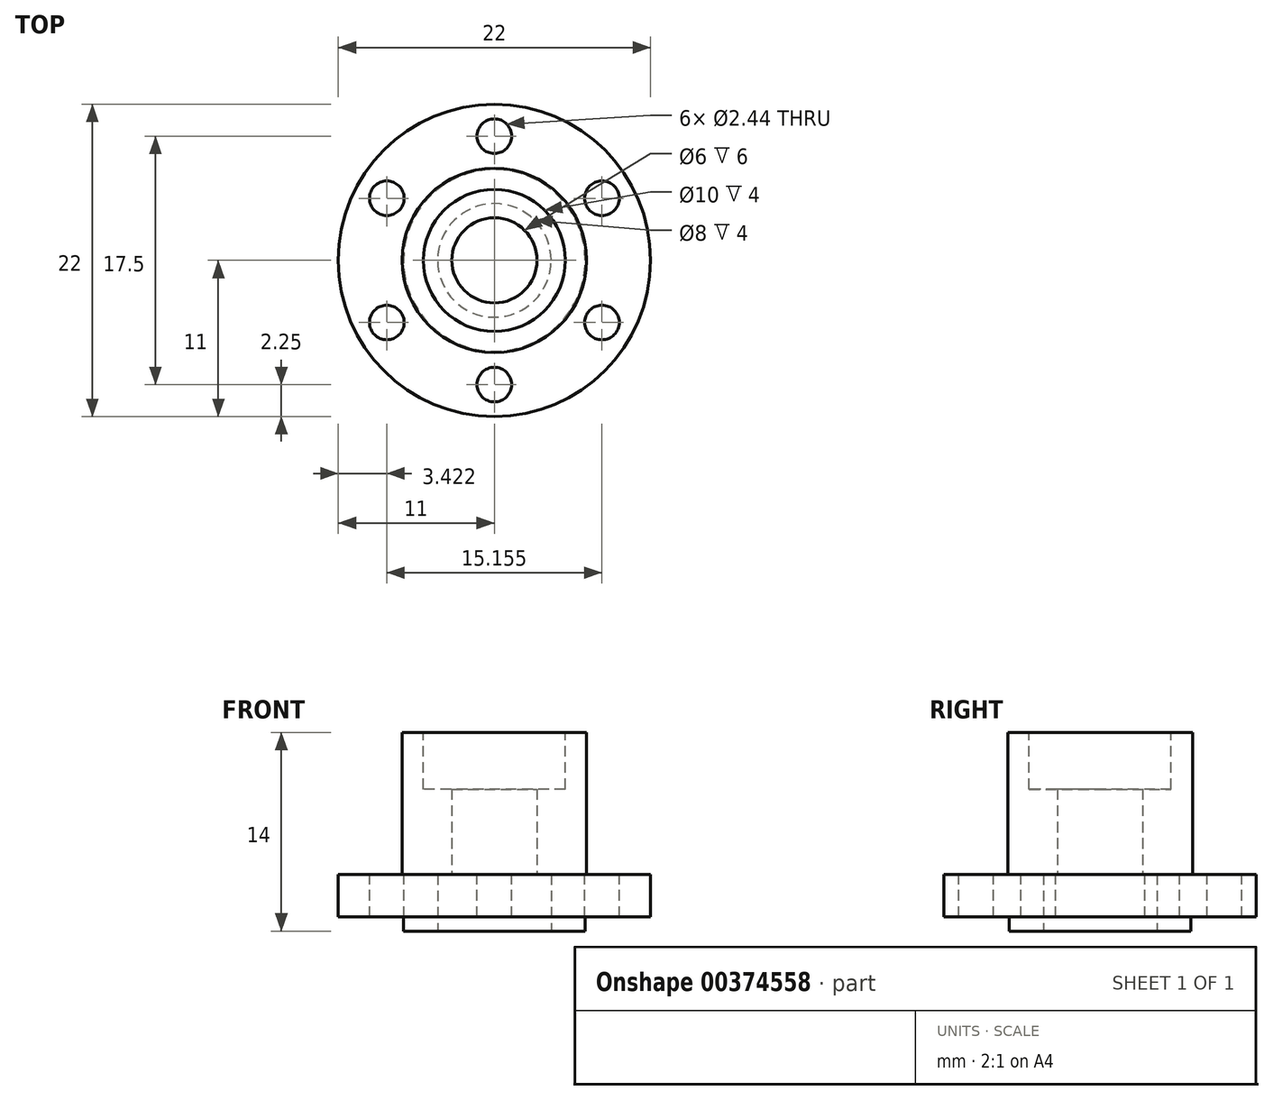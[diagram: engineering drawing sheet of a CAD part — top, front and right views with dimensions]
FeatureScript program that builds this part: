
annotation { "Feature Type Name" : "Feature", "Feature Type Description" : "" }
export const myFeature = defineFeature(function(context is Context, id is Id, definition is map)
    precondition{}
    {
        {
            var Q0;
            Q0=qCreatedBy(makeId("Top.planeOp"),FACE);
            var sketch = newSketch(context, id + "F0", { "sketchPlane" : qUnion([Q0])});
            skCircle(sketch, "E0", {"center": v(0, 0) * mm, "radius": 11 * mm});
            skCircle(sketch, "E1.cCircle", {"center": v(0, 0) * mm, "radius": 7.58 * mm, "construction": true});
            skLineSegment(sketch, "E1.0", {"start": v(7.58, -4.38) * mm, "end": v(0, -8.75) * mm});
            skLineSegment(sketch, "E1.1", {"start": v(0, -8.75) * mm, "end": v(-7.58, -4.38) * mm});
            skLineSegment(sketch, "E1.2", {"start": v(-7.58, -4.37) * mm, "end": v(-7.58, 4.38) * mm});
            skLineSegment(sketch, "E1.3", {"start": v(-7.58, 4.38) * mm, "end": v(0, 8.75) * mm});
            skLineSegment(sketch, "E1.4", {"start": v(0, 8.75) * mm, "end": v(7.58, 4.37) * mm});
            skLineSegment(sketch, "E1.5", {"start": v(7.58, 4.37) * mm, "end": v(7.58, -4.38) * mm});
            skPoint(sketch, "E1.0.midPoint", {"position": v(3.79, -6.56) * mm});
            skSolve(sketch);
        }
        {
            var Q0;
            Q0=makeQuery(id+"F0.imprint","IMPRINT",FACE,{"disambiguationData":[TD([[makeQuery(id+"F0.imprint","IMPRINT",EDGE,{"derivedFrom":sQuery(id+"F0.wireOp",EDGE,"E0")}),1.0]])]});
            var Q1;
            Q1=makeQuery(id+"F0.imprint","IMPRINT",FACE,{"disambiguationData":[TD([[makeQuery(id+"F0.imprint","IMPRINT",EDGE,{"derivedFrom":sQuery(id+"F0.wireOp",EDGE,"E1.0")}),-1.0]])]});
            extrude(context, id + "F1", {"entities" : qUnion([Q0, Q1]), "depth" : 3 * mm});
        }
        {
            var Q0;
            Q0=makeQuery(id+"F1.opExtrude","CAP_FACE",FACE,{"disambiguationData":[OSD([sQuery(id+"F0.wireOp",EDGE,"E0")])],"isStart":false});
            var sketch = newSketch(context, id + "F2", { "sketchPlane" : qUnion([Q0])});
            skCircle(sketch, "E2.cCircle", {"center": v(0, 0) * mm, "radius": 7.58 * mm, "construction": true});
            skLineSegment(sketch, "E2.0", {"start": v(7.58, -4.38) * mm, "end": v(0, -8.75) * mm});
            skLineSegment(sketch, "E2.1", {"start": v(0, -8.75) * mm, "end": v(-7.58, -4.37) * mm});
            skLineSegment(sketch, "E2.2", {"start": v(-7.58, -4.38) * mm, "end": v(-7.58, 4.38) * mm});
            skLineSegment(sketch, "E2.3", {"start": v(-7.58, 4.38) * mm, "end": v(0, 8.75) * mm});
            skLineSegment(sketch, "E2.4", {"start": v(0, 8.75) * mm, "end": v(7.58, 4.37) * mm});
            skLineSegment(sketch, "E2.5", {"start": v(7.58, 4.37) * mm, "end": v(7.58, -4.38) * mm});
            skPoint(sketch, "E2.0.midPoint", {"position": v(3.79, -6.56) * mm});
            skSolve(sketch);
        }
        {
            var Q0;
            Q0=sQuery(id+"F2.wireOp",VERTEX,"E2.4.start");
            var Q1;
            Q1=sQuery(id+"F2.wireOp",VERTEX,"E2.5.start");
            var Q2;
            Q2=sQuery(id+"F2.wireOp",VERTEX,"E2.0.start");
            var Q3;
            Q3=sQuery(id+"F2.wireOp",VERTEX,"E2.1.start");
            var Q4;
            Q4=sQuery(id+"F2.wireOp",VERTEX,"E2.2.start");
            var Q5;
            Q5=sQuery(id+"F2.wireOp",VERTEX,"E2.3.start");
            var Q6;
            Q6=makeQuery(id+"F1.opExtrude","SWEPT_BODY",BODY,{"disambiguationData":[OSD([sQuery(id+"F0.wireOp",EDGE,"E0")])]});
            hole(context, id + "F3", {"style" : HoleStyle.SIMPLE, "endStyle" : HoleEndStyle.THROUGH, "standardTappedOrClearance" : lookupTablePath({ "standard" : "ANSI", "fit" : "Normal (ASME)", "size" : "#2", "type" : "Clearance" }), "standardBlindInLast" : lookupTablePath({ "fit" : "Free", "standard" : "ANSI", "size" : "#2", "type" : "Clearance" }), "holeDiameter" : 2.44 * mm, "isTappedThrough" : true, "tappedDepth" : 12 * mm, "tapClearance" : 3, "locations" : qUnion([Q0, Q1, Q2, Q3, Q4, Q5]), "scope" : qUnion([Q6])});
        }
        {
            var Q0;
            Q0=makeQuery(id+"F1.opExtrude","CAP_FACE",FACE,{"disambiguationData":[OSD([sQuery(id+"F0.wireOp",EDGE,"E0")])],"isStart":false});
            var sketch = newSketch(context, id + "F4", { "sketchPlane" : qUnion([Q0])});
            skCircle(sketch, "E3", {"center": v(0, 0) * mm, "radius": 6.5 * mm});
            skCircle(sketch, "E4", {"center": v(0, 0) * mm, "radius": 4 * mm});
            skSolve(sketch);
        }
        {
            var Q0;
            Q0=makeQuery(id+"F4.imprint","IMPRINT",FACE,{"disambiguationData":[TD([[makeQuery(id+"F4.imprint","IMPRINT",EDGE,{"derivedFrom":sQuery(id+"F4.wireOp",EDGE,"E3")}),1.0]])]});
            var Q1;
            Q1=makeQuery(id+"F4.imprint","IMPRINT",FACE,{"disambiguationData":[TD([[makeQuery(id+"F4.imprint","IMPRINT",EDGE,{"derivedFrom":sQuery(id+"F4.wireOp",EDGE,"E4")}),1.0]])]});
            extrude(context, id + "F5", {"entities" : qUnion([Q0, Q1]), "operationType" : NewBodyOperationType.ADD, "depth" : 10 * mm});
        }
        {
            var Q0;
            Q0=makeQuery(id+"F1.opExtrude","CAP_FACE",FACE,{"disambiguationData":[OSD([sQuery(id+"F0.wireOp",EDGE,"E0")])],"isStart":true});
            var sketch = newSketch(context, id + "F6", { "sketchPlane" : qUnion([Q0])});
            skCircle(sketch, "E5", {"center": v(0, 0) * mm, "radius": 5 * mm});
            skCircle(sketch, "E6", {"center": v(0, 0) * mm, "radius": 3 * mm});
            skSolve(sketch);
        }
        {
            var Q0;
            Q0=makeQuery(id+"F6.imprint","IMPRINT",FACE,{"disambiguationData":[TD([[makeQuery(id+"F6.imprint","IMPRINT",EDGE,{"derivedFrom":sQuery(id+"F6.wireOp",EDGE,"E6")}),1.0]])]});
            extrude(context, id + "F7", {"entities" : qUnion([Q0]), "operationType" : NewBodyOperationType.REMOVE, "endBound" : BoundingType.THROUGH_ALL, "oppositeDirection" : true, "depth" : 25 * mm});
        }
        {
            var Q0;
            Q0=makeQuery(id+"F5.opExtrude","CAP_FACE",FACE,{"disambiguationData":[OSD([sQuery(id+"F4.wireOp",EDGE,"E3")])],"isStart":false});
            var sketch = newSketch(context, id + "F8", { "sketchPlane" : qUnion([Q0])});
            skCircle(sketch, "E7", {"center": v(0, 0) * mm, "radius": 5 * mm});
            skSolve(sketch);
        }
        {
            var Q0;
            Q0=makeQuery(id+"F8.imprint","IMPRINT",FACE,{"disambiguationData":[TD([[makeQuery(id+"F8.imprint","IMPRINT",EDGE,{"derivedFrom":sQuery(id+"F8.wireOp",EDGE,"E7")}),1.0]])]});
            extrude(context, id + "F9", {"entities" : qUnion([Q0]), "operationType" : NewBodyOperationType.REMOVE, "oppositeDirection" : true, "depth" : 4 * mm});
        }
        {
            var Q0;
            Q0=qCreatedBy(makeId("Top.planeOp"),FACE);
            var sketch = newSketch(context, id + "F10", { "sketchPlane" : qUnion([Q0])});
            skCircle(sketch, "E8", {"center": v(0, 0) * mm, "radius": 6.4 * mm});
            skSolve(sketch);
        }
        {
            var Q0;
            Q0=makeQuery(id+"F10.imprint","IMPRINT",FACE,{"disambiguationData":[TD([[makeQuery(id+"F10.imprint","IMPRINT",EDGE,{"derivedFrom":sQuery(id+"F10.wireOp",EDGE,"E8")}),1.0]])]});
            extrude(context, id + "F11", {"entities" : qUnion([Q0]), "operationType" : NewBodyOperationType.ADD, "oppositeDirection" : true, "depth" : 1 * mm});
        }
        {
            var Q0;
            Q0=makeQuery(id+"F11.opExtrude","CAP_FACE",FACE,{"disambiguationData":[OSD([sQuery(id+"F10.wireOp",EDGE,"E8")])],"isStart":false});
            var sketch = newSketch(context, id + "F12", { "sketchPlane" : qUnion([Q0])});
            skCircle(sketch, "E9", {"center": v(0, 0) * mm, "radius": 4 * mm});
            skSolve(sketch);
        }
        {
            var Q0;
            Q0=makeQuery(id+"F12.imprint","IMPRINT",FACE,{"disambiguationData":[TD([[makeQuery(id+"F12.imprint","IMPRINT",EDGE,{"derivedFrom":sQuery(id+"F12.wireOp",EDGE,"E9")}),1.0]])]});
            extrude(context, id + "F13", {"entities" : qUnion([Q0]), "operationType" : NewBodyOperationType.REMOVE, "oppositeDirection" : true, "depth" : 4 * mm});
        }
    });
